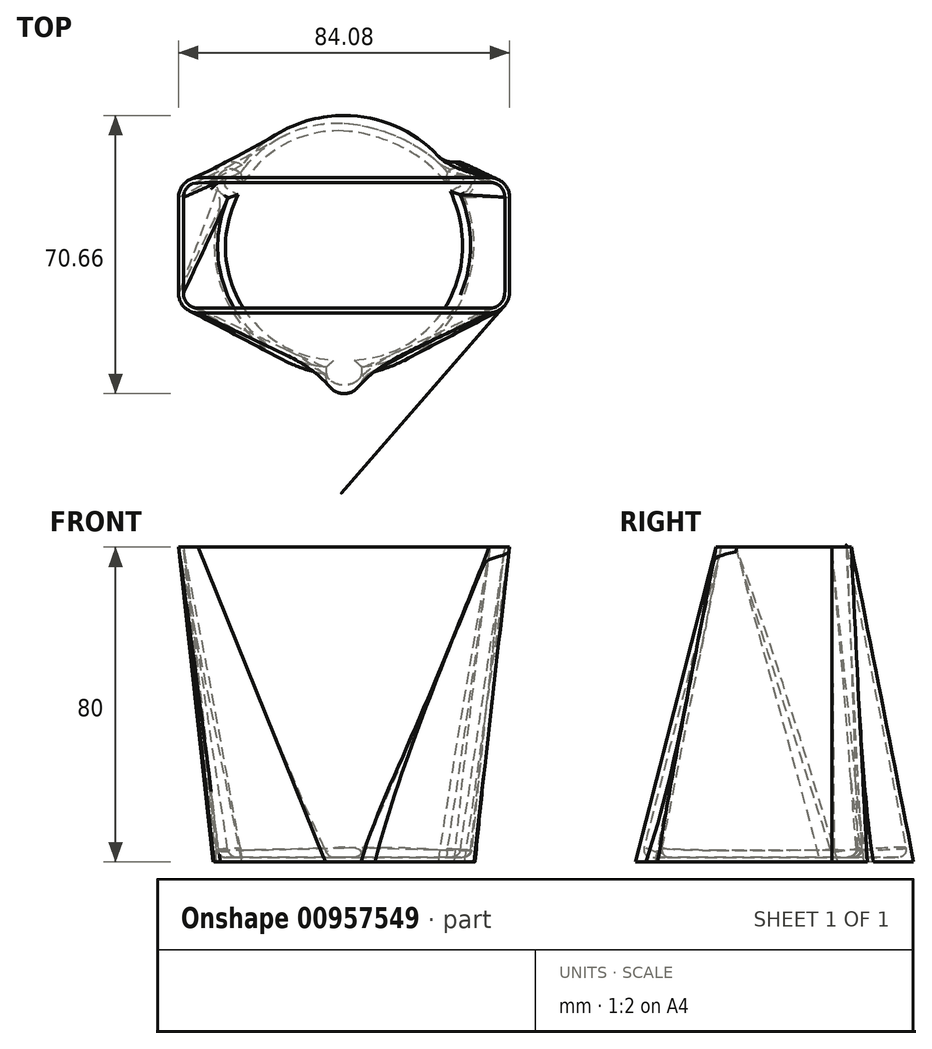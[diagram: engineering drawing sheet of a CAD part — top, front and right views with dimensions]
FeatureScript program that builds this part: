
annotation { "Feature Type Name" : "Feature", "Feature Type Description" : "" }
export const myFeature = defineFeature(function(context is Context, id is Id, definition is map)
    precondition{}
    {
        {
            var Q0;
            Q0=qCreatedBy(makeId("Top.planeOp"),FACE);
            var sketch = newSketch(context, id + "F0", { "sketchPlane" : qUnion([Q0])});
            skArc(sketch, "E0", {"start": v(4.69, -32.65) * mm, "mid": v(28.57, -16.5) * mm, "end": v(30.62, 12.27) * mm});
            skPoint(sketch, "E1", {"position": v(-21.9, 24.67) * mm});
            skPoint(sketch, "E2", {"position": v(24.2, 22.41) * mm});
            skPoint(sketch, "E3", {"position": v(23.77, -22.87) * mm});
            skPoint(sketch, "E4", {"position": v(-24.97, -21.56) * mm});
            skArc(sketch, "E5", {"start": v(-4.69, -32.65) * mm, "mid": v(0, -37.68) * mm, "end": v(4.69, -32.65) * mm});
            skArc(sketch, "E6.1.0", {"start": v(30.62, 12.27) * mm, "mid": v(32.63, 18.84) * mm, "end": v(25.93, 20.38) * mm});
            skArc(sketch, "E6.2.0", {"start": v(-25.93, 20.38) * mm, "mid": v(-32.63, 18.84) * mm, "end": v(-30.62, 12.27) * mm});
            skArc(sketch, "E7.trimOffspring", {"start": v(-30.62, 12.27) * mm, "mid": v(-28.57, -16.5) * mm, "end": v(-4.69, -32.65) * mm});
            skArc(sketch, "E8.trimOffspring", {"start": v(25.93, 20.38) * mm, "mid": v(0, 32.98) * mm, "end": v(-25.93, 20.38) * mm});
            skSolve(sketch);
        }
        {
            var Q0;
            Q0=qCreatedBy(makeId("Top.planeOp"),FACE);
            cPlane(context, id + "F1", {"entities" : qUnion([Q0]), "cplaneType" : CPlaneType.OFFSET, "offset" : 80 * mm, "width" : 150 * mm, "height" : 150 * mm});
        }
        {
            var Q0;
            Q0=qCreatedBy(id+"F1.planeOp",FACE);
            var sketch = newSketch(context, id + "F2", { "sketchPlane" : qUnion([Q0])});
            skLineSegment(sketch, "E9.bottom", {"start": v(37.04, 17.19) * mm, "end": v(-37.04, 17.19) * mm});
            skLineSegment(sketch, "E9.top", {"start": v(37.04, -17.19) * mm, "end": v(-37.04, -17.19) * mm});
            skLineSegment(sketch, "E9.left", {"start": v(42.04, 12.19) * mm, "end": v(42.04, -12.19) * mm});
            skLineSegment(sketch, "E9.right", {"start": v(-42.04, 12.19) * mm, "end": v(-42.04, -12.19) * mm});
            skPoint(sketch, "E9.middle", {"position": v(0, 0) * mm});
            skPoint(sketch, "E10.visualSharp", {"position": v(42.04, 17.19) * mm});
            skArc(sketch, "E10.filletArc", {"start": v(42.04, 12.19) * mm, "mid": v(40.58, 15.72) * mm, "end": v(37.04, 17.19) * mm});
            skPoint(sketch, "E11.visualSharp", {"position": v(42.04, -17.19) * mm});
            skArc(sketch, "E11.filletArc", {"start": v(37.04, -17.19) * mm, "mid": v(40.58, -15.72) * mm, "end": v(42.04, -12.19) * mm});
            skPoint(sketch, "E12.visualSharp", {"position": v(-42.04, -17.19) * mm});
            skArc(sketch, "E12.filletArc", {"start": v(-42.04, -12.19) * mm, "mid": v(-40.58, -15.72) * mm, "end": v(-37.04, -17.19) * mm});
            skPoint(sketch, "E13.visualSharp", {"position": v(-42.04, 17.19) * mm});
            skArc(sketch, "E13.filletArc", {"start": v(-37.04, 17.19) * mm, "mid": v(-40.58, 15.72) * mm, "end": v(-42.04, 12.19) * mm});
            skSolve(sketch);
        }
        {
            var Q0;
            Q0=makeQuery(id+"F0.imprint","IMPRINT",FACE,{"disambiguationData":[TD([[makeQuery(id+"F0.imprint","IMPRINT",EDGE,{"derivedFrom":sQuery(id+"F0.wireOp",EDGE,"E0")}),1.0]])]});
            var Q1;
            Q1=makeQuery(id+"F2.imprint","IMPRINT",FACE,{"disambiguationData":[TD([[makeQuery(id+"F2.imprint","IMPRINT",EDGE,{"derivedFrom":sQuery(id+"F2.wireOp",EDGE,"E9.bottom")}),1.0]])]});
            loft(context, id + "F3", {"sheetProfilesArray" : [{ "sheetProfileEntities" : qUnion([Q0]) }, { "sheetProfileEntities" : qUnion([Q1]) }]});
        }
        {
            var Q0;
            Q0=makeQuery(id+"F3.opLoft","CAP_FACE",FACE,{"disambiguationData":[OSD([makeQuery(id+"F2.imprint","IMPRINT",FACE,{"disambiguationData":[TD([[makeQuery(id+"F2.imprint","IMPRINT",EDGE,{"derivedFrom":sQuery(id+"F2.wireOp",EDGE,"E9.bottom")}),1.0]])]})])],"isStart":true});
            shell(context, id + "F4", {"entities" : qUnion([Q0]), "thickness" : 1.2 * mm});
        }
        {
            var Q0;
            Q0=makeQuery(id+"F3.opLoft","SWEPT_EDGE",EDGE,{"disambiguationData":[OSD([sQuery(id+"F0.wireOp",EDGE,"E6.1.0"),sQuery(id+"F0.wireOp",EDGE,"E8.trimOffspring"),sQuery(id+"F2.wireOp",EDGE,"E9.bottom"),sQuery(id+"F2.wireOp",EDGE,"E13.filletArc")])]});
            var Q1;
            Q1=makeQuery(id+"F3.opLoft","SWEPT_EDGE",EDGE,{"disambiguationData":[OSD([sQuery(id+"F0.wireOp",EDGE,"E6.2.0"),sQuery(id+"F0.wireOp",EDGE,"E7.trimOffspring"),sQuery(id+"F2.wireOp",EDGE,"E9.right"),sQuery(id+"F2.wireOp",EDGE,"E12.filletArc")])]});
            var Q2;
            Q2=makeQuery(id+"F3.opLoft","SWEPT_EDGE",EDGE,{"disambiguationData":[OSD([sQuery(id+"F0.wireOp",EDGE,"E0"),sQuery(id+"F0.wireOp",EDGE,"E5"),sQuery(id+"F2.wireOp",EDGE,"E9.top"),sQuery(id+"F2.wireOp",EDGE,"E11.filletArc")])]});
            fillet(context, id + "F5", {"entities" : qUnion([Q0, Q1, Q2]), "radius" : 5 * mm, "tangentPropagation" : true, "allowEdgeOverflow" : false});
        }
        {
            var Q0;
            Q0=makeQuery(id+"F4.opShell","OFFSET_FACE",FACE,{"disambiguationData":[OSD([makeQuery(id+"F0.imprint","IMPRINT",FACE,{"disambiguationData":[TD([[makeQuery(id+"F0.imprint","IMPRINT",EDGE,{"derivedFrom":sQuery(id+"F0.wireOp",EDGE,"E0")}),1.0]])]})])]});
            fillet(context, id + "F6", {"entities" : qUnion([Q0]), "radius" : 2 * mm, "tangentPropagation" : true, "allowEdgeOverflow" : false});
        }
    });
